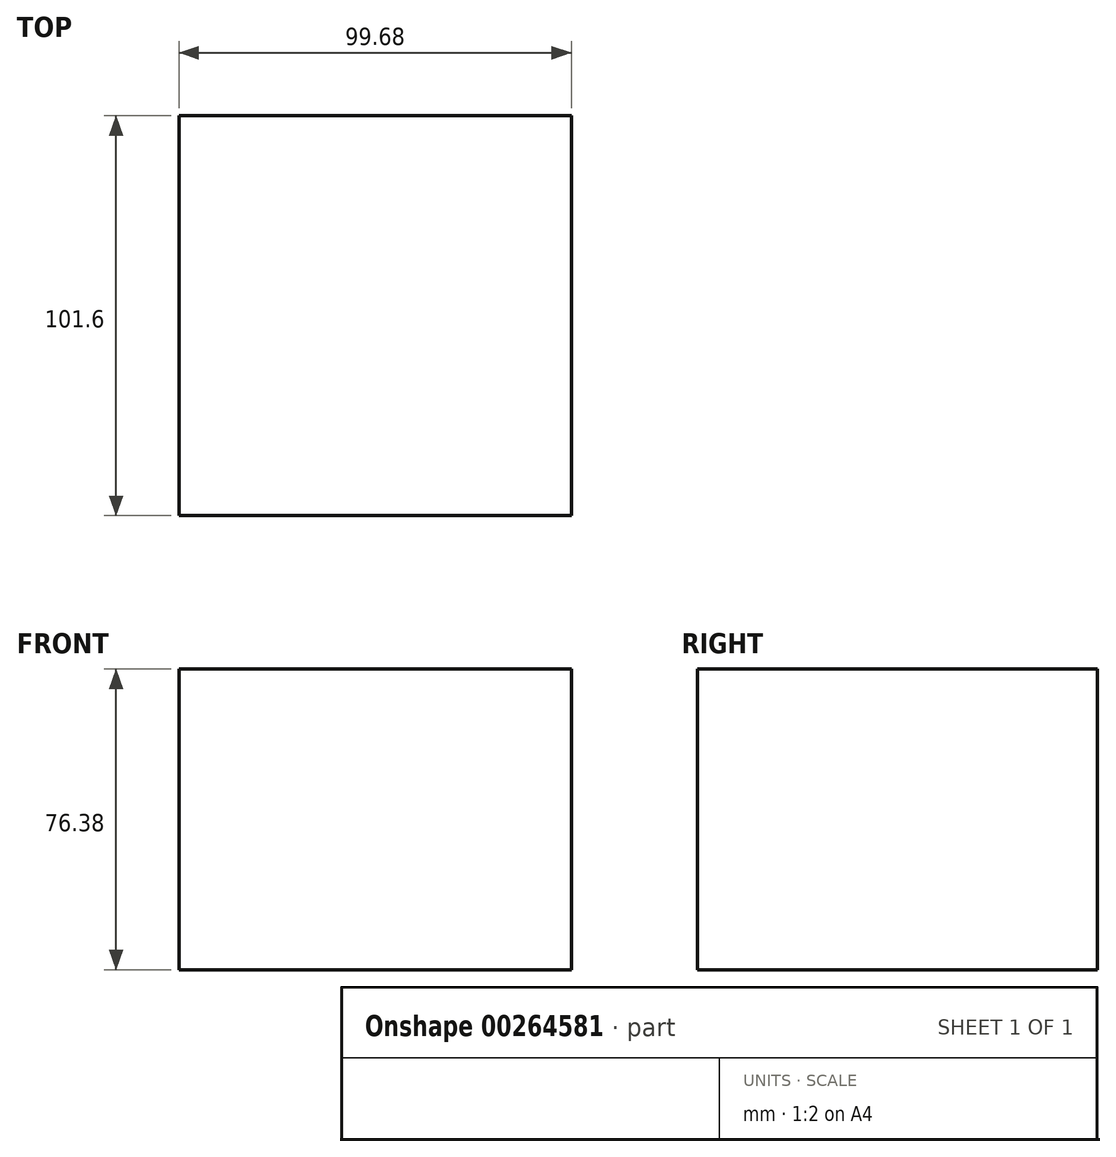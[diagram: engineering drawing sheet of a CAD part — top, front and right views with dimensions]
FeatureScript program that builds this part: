
annotation { "Feature Type Name" : "Feature", "Feature Type Description" : "" }
export const myFeature = defineFeature(function(context is Context, id is Id, definition is map)
    precondition{}
    {
        {
            var Q0;
            Q0=qCreatedBy(makeId("Front.planeOp"),FACE);
            var sketch = newSketch(context, id + "F0", { "sketchPlane" : qUnion([Q0])});
            skLineSegment(sketch, "E0.bottom", {"start": v(0, 0) * mm, "end": v(-99.68, 0) * mm});
            skLineSegment(sketch, "E0.top", {"start": v(0, 76.38) * mm, "end": v(-99.68, 76.38) * mm});
            skLineSegment(sketch, "E0.left", {"start": v(0, 0) * mm, "end": v(0, 76.38) * mm});
            skLineSegment(sketch, "E0.right", {"start": v(-99.68, 0) * mm, "end": v(-99.68, 76.38) * mm});
            skSolve(sketch);
        }
        {
            var Q0;
            Q0=makeQuery(id+"F0.imprint","IMPRINT",FACE,{"disambiguationData":[TD([[makeQuery(id+"F0.imprint","IMPRINT",EDGE,{"derivedFrom":sQuery(id+"F0.wireOp",EDGE,"E0.bottom")}),-1.0]])]});
            extrude(context, id + "F1", {"entities" : qUnion([Q0]), "depth" : 101.6 * mm});
        }
        {
            var Q0;
            Q0=makeQuery(id+"F1.opExtrude","SWEPT_FACE",FACE,{"disambiguationData":[OSD([sQuery(id+"F0.wireOp",EDGE,"E0.top")])]});
            var sketch = newSketch(context, id + "F2", { "sketchPlane" : qUnion([Q0])});
            skCircle(sketch, "E1", {"center": v(-90.16, -10.03) * mm, "radius": 6.52 * mm});
            skSolve(sketch);
        }
        {
            var Q0;
            Q0=sQuery(id+"F2.wireOp",EDGE,"E1");
            extrude(context, id + "F3", {"bodyType" : ToolBodyType.SURFACE, "surfaceEntities" : qUnion([Q0]), "depth" : 101.6 * mm});
        }
    });
